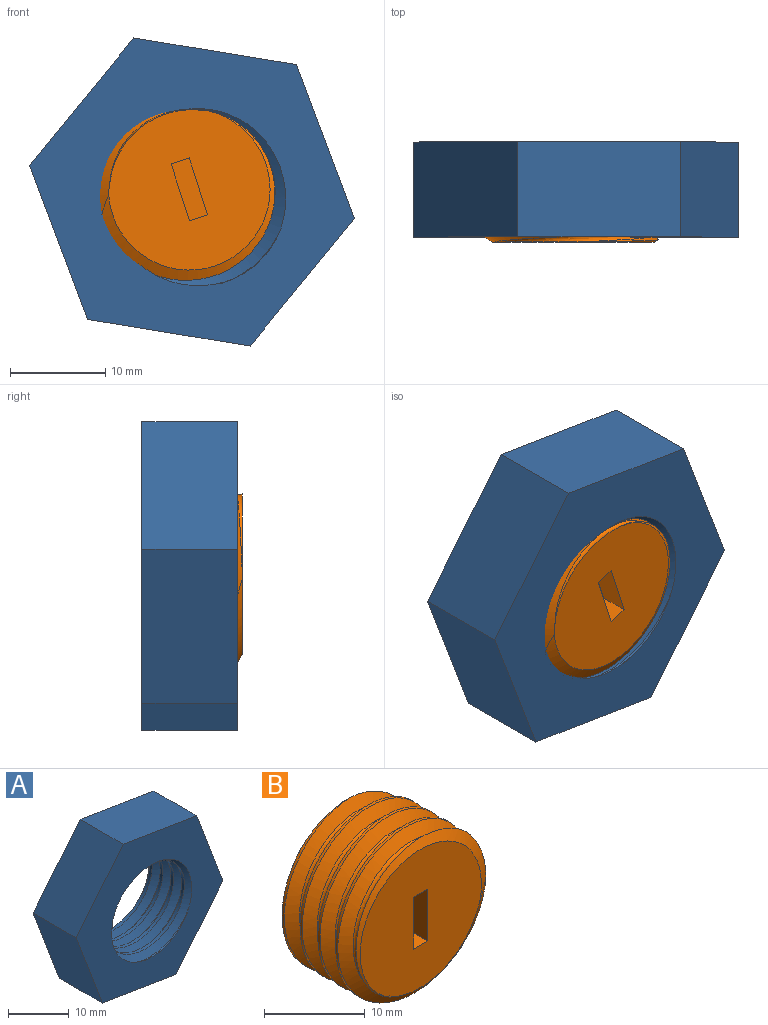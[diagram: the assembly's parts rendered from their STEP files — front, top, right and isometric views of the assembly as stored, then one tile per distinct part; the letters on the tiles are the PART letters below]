
ASSEMBLY  parts=2 mates=1
PART A: 12 faces, bbox 34.9x12.8x33.2 mm
  f0: plane 13.4x10.98mm, normal (0.77,0,-0.63), area 173.2mm2, adj f1,f5,f6,f7
  f1: plane 16.21x10mm, normal (0.94,0,0.35), area 173.2mm2, adj f0,f2,f6,f7
  f2: plane 17.09x10mm, normal (0.16,0,0.99), area 173.2mm2, adj f1,f3,f6,f7
  f3: plane 13.4x10.98mm, normal (-0.77,0,0.63), area 173.2mm2, adj f2,f4,f6,f7
  f4: plane 16.21x10mm, normal (-0.94,0,-0.35), area 173.2mm2, adj f3,f5,f6,f7
  f5: plane 17.09x10mm, normal (-0.16,0,-0.99), area 173.2mm2, adj f0,f4,f6,f7
  f6: plane 34.94x33.17mm, normal (0,-1,0), area 504mm2, adj f0,f1,f2,f3,f4,f5,f8,f9
  f7: plane 34.94x33.17mm, normal (0,1,0), area 504mm2, adj f0,f1,f2,f3,f4,f5,f8,f9
  f8: bspline ~23.33x20.21mm, area 370.7mm2, adj f6,f7,f10,f11
  f9: bspline ~23.33x20.21mm, area 370.3mm2, adj f6,f7,f10,f11
  f10: bspline ~23.59x20.43mm, area 92.4mm2, adj f6,f7,f8,f9
  f11: cylinder r=8.75mm len=17.5mm, axis (0,-1,0), area 138.7mm2, adj f6,f7,f8,f9
PART B: 12 faces, bbox 23.2x12.8x20.2 mm
  f0: plane 17.11x16.91mm, normal (0,-1,0), area 211.6mm2, adj f3,f4,f5,f6,f7,f8,f9,f10
  f1: cylinder r=9.75mm len=19.5mm, axis (0,1,0), area 80.1mm2, adj f2,f4,f5,f6
  f2: plane 18.75x18.65mm, normal (0,1,0), area 253.4mm2, adj f1,f3,f4,f5
  f3: bspline ~19.39x16.79mm, area 146.2mm2, adj f0,f2,f4,f5
  f4: bspline ~22.52x19.5mm, area 345.6mm2, adj f0,f1,f2,f3,f6
  f5: bspline ~22.52x19.5mm, area 345.8mm2, adj f0,f1,f2,f3,f6
  f6: cone r=9.75mm half-angle=63.4deg, axis (0,1,0), area 32.6mm2, adj f0,f1,f4,f5
  f7: plane 6.3x3mm, normal (1,0,0), area 18.9mm2, adj f0,f8,f10,f11
  f8: plane 3x2mm, normal (0,0,1), area 6mm2, adj f0,f7,f9,f11
  f9: plane 6.3x3mm, normal (-1,0,0), area 18.9mm2, adj f0,f8,f10,f11
  f10: plane 3x2mm, normal (0,0,-1), area 6mm2, adj f0,f7,f9,f11
  f11: plane 6.3x2mm, normal (0,-1,0), area 12.6mm2, adj f7,f8,f9,f10
PLACE A t=(-48.32,0,-3.75)mm
PLACE B rot(axis=(0,1,0),162.1deg) t=(-18.61,-0.52,-3.47)mm
MATE cylindrical A.f6 <-> B.f1  axis (0,-1,0) through (-18.61,-10,-3.47)mm
